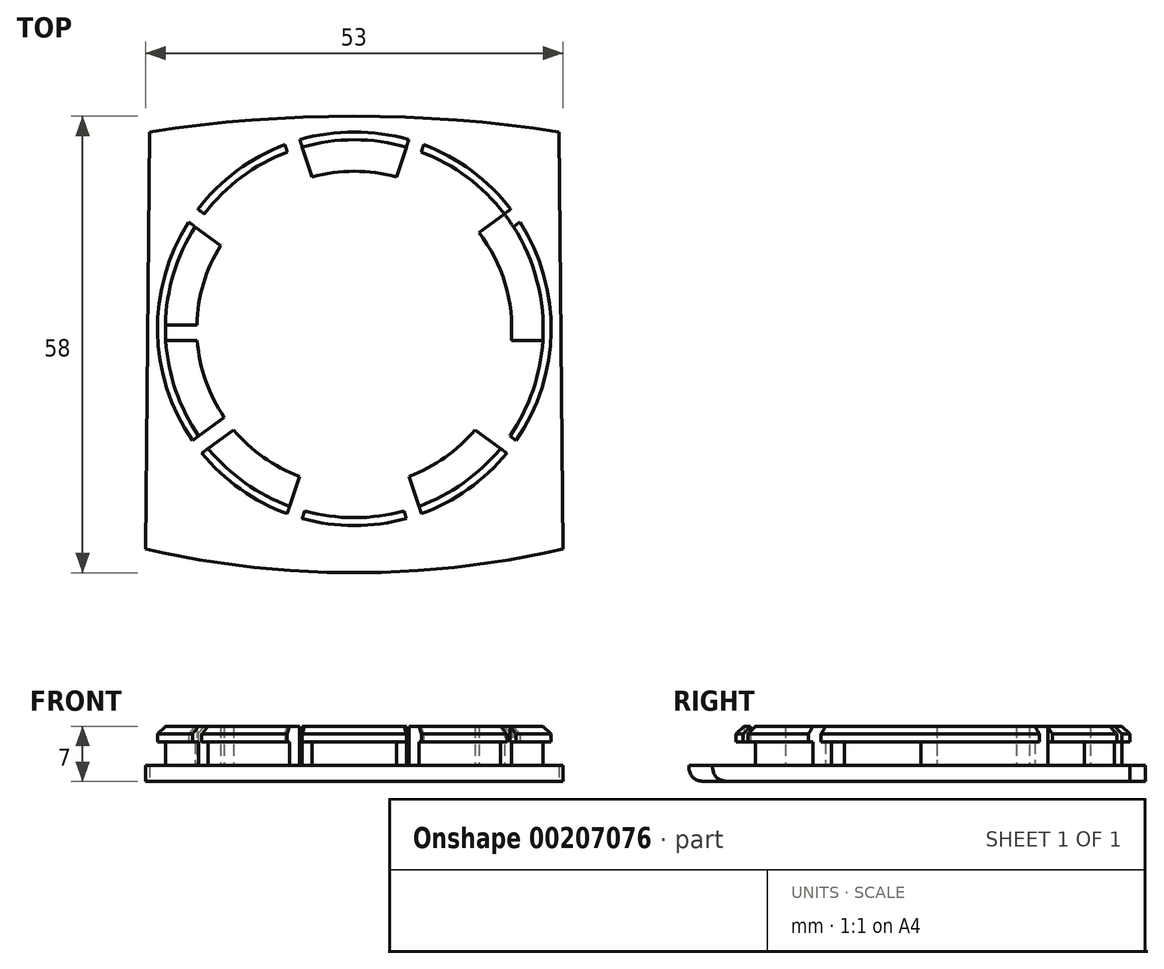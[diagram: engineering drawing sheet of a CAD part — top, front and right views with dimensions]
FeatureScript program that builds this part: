
annotation { "Feature Type Name" : "Feature", "Feature Type Description" : "" }
export const myFeature = defineFeature(function(context is Context, id is Id, definition is map)
    precondition{}
    {
        {
            var Q0;
            Q0=qCreatedBy(makeId("Top.planeOp"),FACE);
            var sketch = newSketch(context, id + "F0", { "sketchPlane" : qUnion([Q0])});
            skLineSegment(sketch, "E0", {"start": v(-26, 27.5) * mm, "end": v(-26.5, -27.5) * mm});
            skLineSegment(sketch, "E1", {"start": v(-26.5, -27.5) * mm, "end": v(26.5, -27.5) * mm, "construction": true});
            skLineSegment(sketch, "E2", {"start": v(26.5, -27.5) * mm, "end": v(26, 27.5) * mm});
            skLineSegment(sketch, "E3", {"start": v(26, 27.5) * mm, "end": v(-26, 27.5) * mm});
            skArc(sketch, "E4", {"start": v(-26.5, -27.5) * mm, "mid": v(0, -30.5) * mm, "end": v(26.5, -27.5) * mm});
            skPoint(sketch, "E5", {"position": v(0, -27.5) * mm});
            skPoint(sketch, "E6", {"position": v(0, 27.5) * mm});
            skLineSegment(sketch, "E7", {"start": v(0, 27.5) * mm, "end": v(0, -27.5) * mm, "construction": true});
            skPoint(sketch, "E8", {"position": v(-26.25, 0) * mm});
            skPoint(sketch, "E9", {"position": v(26.25, 0) * mm});
            skLineSegment(sketch, "E10", {"start": v(-26.25, 0) * mm, "end": v(26.25, 0) * mm, "construction": true});
            skPoint(sketch, "E11", {"position": v(0, 0) * mm});
            skArc(sketch, "E12", {"start": v(26.02, 25.5) * mm, "mid": v(0, 27.5) * mm, "end": v(-26.02, 25.5) * mm});
            skSolve(sketch);
        }
        {
            var Q0;
            {var subQ4=sQuery(id+"F0.wireOp",EDGE,"E4");Q0=makeQuery(id+"F0.imprint","IMPRINT",FACE,{"disambiguationData":[TD([[makeQuery(id+"F0.imprint","IMPRINT",EDGE,{"derivedFrom":subQ4}),1.0]])]});}
            extrude(context, id + "F1", {"entities" : qUnion([Q0]), "depth" : 2 * mm});
        }
        {
            var Q0;
            Q0=qCreatedBy(makeId("Top.planeOp"),FACE);
            var sketch = newSketch(context, id + "F2", { "sketchPlane" : qUnion([Q0])});
            skCircle(sketch, "E13", {"center": v(0, 0.5) * mm, "radius": 24 * mm});
            skCircle(sketch, "E14.0", {"center": v(0, 0.5) * mm, "radius": 20 * mm});
            skSolve(sketch);
        }
        {
            var Q0;
            Q0=makeQuery(id+"F2.imprint","IMPRINT",FACE,{"disambiguationData":[TD([[makeQuery(id+"F2.imprint","IMPRINT",EDGE,{"derivedFrom":sQuery(id+"F2.wireOp",EDGE,"E13")}),1.0]])]});
            extrude(context, id + "F3", {"entities" : qUnion([Q0]), "operationType" : NewBodyOperationType.ADD, "depth" : 7 * mm});
        }
        {
            var Q0;
            {var subQ0=sQuery(id+"F0.wireOp",EDGE,"E4");var subQ1=sQuery(id+"F0.wireOp",EDGE,"E3");var subQ2=sQuery(id+"F0.wireOp",EDGE,"E2");var subQ3=sQuery(id+"F0.wireOp",EDGE,"E0");Q0=makeQuery(id+"F3.boolean.opBoolean","SPLIT",FACE,{"disambiguationData":[TD([makeQuery(id+"F1.opExtrude","SWEPT_FACE",FACE,{"disambiguationData":[OSD([subQ3])]})])],"derivedFrom":makeQuery(id+"F1.opExtrude","CAP_FACE",FACE,{"disambiguationData":[OSD([subQ3,subQ2,subQ1,subQ0])],"isStart":false})});}
            cPlane(context, id + "F4", {"entities" : qUnion([Q0]), "cplaneType" : CPlaneType.OFFSET, "offset" : 3 * mm, "width" : 150 * mm, "height" : 150 * mm});
        }
        {
            var Q0;
            Q0=qCreatedBy(id+"F4.planeOp",FACE);
            var sketch = newSketch(context, id + "F5", { "sketchPlane" : qUnion([Q0])});
            skCircle(sketch, "E15.0", {"center": v(0, 0.5) * mm, "radius": 25 * mm});
            skCircle(sketch, "E16.0", {"center": v(0, 0.5) * mm, "radius": 23.82 * mm});
            skSolve(sketch);
        }
        {
            var Q0;
            Q0=makeQuery(id+"F5.imprint","IMPRINT",FACE,{"disambiguationData":[TD([[makeQuery(id+"F5.imprint","IMPRINT",EDGE,{"derivedFrom":sQuery(id+"F5.wireOp",EDGE,"E15.0")}),1.0]])]});
            extrude(context, id + "F6", {"entities" : qUnion([Q0]), "operationType" : NewBodyOperationType.ADD, "depth" : 2 * mm});
        }
        {
            var Q0;
            Q0=makeQuery(id+"F6.opExtrude","CAP_EDGE",EDGE,{"disambiguationData":[OSD([sQuery(id+"F5.wireOp",EDGE,"E15.0")])],"isStart":false});
            chamfer(context, id + "F7", {"entities" : qUnion([Q0]), "width" : 1 * mm, "tangentPropagation" : true});
        }
        {
            var Q0;
            {var subQ0=sQuery(id+"F0.wireOp",EDGE,"E4");var subQ1=sQuery(id+"F0.wireOp",EDGE,"E3");var subQ2=sQuery(id+"F0.wireOp",EDGE,"E2");var subQ3=sQuery(id+"F0.wireOp",EDGE,"E0");Q0=makeQuery(id+"F3.boolean.opBoolean","SPLIT",FACE,{"disambiguationData":[TD([makeQuery(id+"F1.opExtrude","SWEPT_FACE",FACE,{"disambiguationData":[OSD([subQ3])]})])],"derivedFrom":makeQuery(id+"F1.opExtrude","CAP_FACE",FACE,{"disambiguationData":[OSD([subQ3,subQ2,subQ1,subQ0])],"isStart":false})});}
            var sketch = newSketch(context, id + "F8", { "sketchPlane" : qUnion([Q0])});
            skLineSegment(sketch, "E17.bottom", {"start": v(26, 1) * mm, "end": v(-26, 1) * mm});
            skLineSegment(sketch, "E17.top", {"start": v(26, -1) * mm, "end": v(-26, -1) * mm});
            skLineSegment(sketch, "E17.left", {"start": v(26, 1) * mm, "end": v(26, -1) * mm});
            skLineSegment(sketch, "E17.right", {"start": v(-26, 1) * mm, "end": v(-26, -1) * mm});
            skPoint(sketch, "E17.middle", {"position": v(0, 0) * mm});
            skLineSegment(sketch, "E18.1.0", {"start": v(21.62, -14.47) * mm, "end": v(-20.45, 16.1) * mm});
            skLineSegment(sketch, "E18.1.1", {"start": v(20.45, -16.1) * mm, "end": v(-21.62, 14.47) * mm});
            skLineSegment(sketch, "E18.1.2", {"start": v(-20.45, 16.1) * mm, "end": v(-21.62, 14.47) * mm});
            skLineSegment(sketch, "E18.1.3", {"start": v(21.62, -14.47) * mm, "end": v(20.45, -16.1) * mm});
            skLineSegment(sketch, "E18.2.0", {"start": v(8.99, -24.42) * mm, "end": v(-7.08, 25.04) * mm});
            skLineSegment(sketch, "E18.2.1", {"start": v(7.08, -25.04) * mm, "end": v(-8.99, 24.42) * mm});
            skLineSegment(sketch, "E18.2.2", {"start": v(-7.08, 25.04) * mm, "end": v(-8.99, 24.42) * mm});
            skLineSegment(sketch, "E18.2.3", {"start": v(8.99, -24.42) * mm, "end": v(7.08, -25.04) * mm});
            skLineSegment(sketch, "E18.3.0", {"start": v(-7.08, -25.04) * mm, "end": v(8.99, 24.42) * mm});
            skLineSegment(sketch, "E18.3.1", {"start": v(-8.99, -24.42) * mm, "end": v(7.08, 25.04) * mm});
            skLineSegment(sketch, "E18.3.2", {"start": v(8.99, 24.42) * mm, "end": v(7.08, 25.04) * mm});
            skLineSegment(sketch, "E18.3.3", {"start": v(-7.08, -25.04) * mm, "end": v(-8.99, -24.42) * mm});
            skLineSegment(sketch, "E18.4.0", {"start": v(-20.45, -16.1) * mm, "end": v(21.62, 14.47) * mm});
            skLineSegment(sketch, "E18.4.1", {"start": v(-21.62, -14.47) * mm, "end": v(20.45, 16.1) * mm});
            skLineSegment(sketch, "E18.4.2", {"start": v(21.62, 14.47) * mm, "end": v(20.45, 16.1) * mm});
            skLineSegment(sketch, "E18.4.3", {"start": v(-20.45, -16.1) * mm, "end": v(-21.62, -14.47) * mm});
            skLineSegment(sketch, "E18.5.0", {"start": v(-26, -1) * mm, "end": v(26, -1) * mm});
            skLineSegment(sketch, "E18.5.1", {"start": v(-26, 1) * mm, "end": v(26, 1) * mm});
            skLineSegment(sketch, "E18.5.2", {"start": v(26, -1) * mm, "end": v(26, 1) * mm});
            skLineSegment(sketch, "E18.5.3", {"start": v(-26, -1) * mm, "end": v(-26, 1) * mm});
            skLineSegment(sketch, "E18.anchor1", {"start": v(0, 0) * mm, "end": v(-26, -1) * mm, "construction": true});
            skLineSegment(sketch, "E18.anchor2", {"start": v(0, 0) * mm, "end": v(26, 1) * mm, "construction": true});
            skSolve(sketch);
        }
        {
            var Q0;
            {var subQ0=sQuery(id+"F8.wireOp",EDGE,"E18.2.1");var subQ1=sQuery(id+"F8.wireOp",EDGE,"E18.1.0");var subQ2=makeQuery(id+"F8.imprint","INTERSECT",VERTEX,{"derivedFrom":[subQ1,subQ0]});Q0=makeQuery(id+"F8.imprint","IMPRINT",FACE,{"disambiguationData":[TD([[makeQuery(id+"F8.imprint","IMPRINT",EDGE,{"disambiguationData":[TD([[subQ2,1.0]])],"derivedFrom":subQ0}),1.0]])]});}
            var Q1;
            {var subQ1=sQuery(id+"F8.wireOp",EDGE,"E18.2.0");var subQ5=sQuery(id+"F8.wireOp",EDGE,"E18.4.1");var subQ9=makeQuery(id+"F8.imprint","INTERSECT",VERTEX,{"derivedFrom":[subQ1,subQ5]});Q1=makeQuery(id+"F8.imprint","IMPRINT",FACE,{"disambiguationData":[TD([[makeQuery(id+"F8.imprint","IMPRINT",EDGE,{"disambiguationData":[TD([[subQ9,-1.0]])],"derivedFrom":subQ1}),-1.0]])]});}
            var Q2;
            {var subQ1=sQuery(id+"F8.wireOp",EDGE,"E18.1.0");var subQ5=sQuery(id+"F8.wireOp",EDGE,"E18.3.1");var subQ9=makeQuery(id+"F8.imprint","INTERSECT",VERTEX,{"derivedFrom":[subQ1,subQ5]});Q2=makeQuery(id+"F8.imprint","IMPRINT",FACE,{"disambiguationData":[TD([[makeQuery(id+"F8.imprint","IMPRINT",EDGE,{"disambiguationData":[TD([[subQ9,-1.0]])],"derivedFrom":subQ1}),-1.0]])]});}
            var Q3;
            {var subQ0=sQuery(id+"F8.wireOp",EDGE,"E18.5.1");var subQ1=sQuery(id+"F8.wireOp",EDGE,"E18.3.0");var subQ2=makeQuery(id+"F8.imprint","INTERSECT",VERTEX,{"derivedFrom":[subQ1,subQ0]});Q3=makeQuery(id+"F8.imprint","IMPRINT",FACE,{"disambiguationData":[TD([[makeQuery(id+"F8.imprint","IMPRINT",EDGE,{"disambiguationData":[TD([[subQ2,-1.0]])],"derivedFrom":subQ1}),-1.0]])]});}
            var Q4;
            {var subQ0=sQuery(id+"F8.wireOp",EDGE,"E18.5.0");var subQ1=sQuery(id+"F8.wireOp",EDGE,"E18.1.0");var subQ2=makeQuery(id+"F8.imprint","INTERSECT",VERTEX,{"derivedFrom":[subQ1,subQ0]});Q4=makeQuery(id+"F8.imprint","IMPRINT",FACE,{"disambiguationData":[TD([[makeQuery(id+"F8.imprint","IMPRINT",EDGE,{"disambiguationData":[TD([[subQ2,-1.0]])],"derivedFrom":subQ1}),-1.0]])]});}
            var Q5;
            {var subQ3=sQuery(id+"F8.wireOp",EDGE,"E18.2.0");var subQ5=sQuery(id+"F8.wireOp",EDGE,"E18.1.1");var subQ6=makeQuery(id+"F8.imprint","INTERSECT",VERTEX,{"derivedFrom":[subQ5,subQ3]});Q5=makeQuery(id+"F8.imprint","IMPRINT",FACE,{"disambiguationData":[TD([[makeQuery(id+"F8.imprint","IMPRINT",EDGE,{"disambiguationData":[TD([[subQ6,-1.0]])],"derivedFrom":subQ3}),-1.0]])]});}
            var Q6;
            {var subQ1=sQuery(id+"F8.wireOp",EDGE,"E18.2.1");var subQ5=sQuery(id+"F8.wireOp",EDGE,"E18.3.0");var subQ9=makeQuery(id+"F8.imprint","INTERSECT",VERTEX,{"derivedFrom":[subQ1,subQ5]});Q6=makeQuery(id+"F8.imprint","IMPRINT",FACE,{"disambiguationData":[TD([[makeQuery(id+"F8.imprint","IMPRINT",EDGE,{"disambiguationData":[TD([[subQ9,-1.0]])],"derivedFrom":subQ1}),1.0]])]});}
            var Q7;
            {var subQ1=sQuery(id+"F8.wireOp",EDGE,"E18.1.1");var subQ7=sQuery(id+"F8.wireOp",EDGE,"E18.2.0");var subQ8=makeQuery(id+"F8.imprint","INTERSECT",VERTEX,{"derivedFrom":[subQ1,subQ7]});Q7=makeQuery(id+"F8.imprint","IMPRINT",FACE,{"disambiguationData":[TD([[makeQuery(id+"F8.imprint","IMPRINT",EDGE,{"disambiguationData":[TD([[subQ8,-1.0]])],"derivedFrom":subQ1}),1.0]])]});}
            var Q8;
            {var subQ1=sQuery(id+"F8.wireOp",EDGE,"E18.3.1");var subQ7=sQuery(id+"F8.wireOp",EDGE,"E18.4.0");var subQ8=makeQuery(id+"F8.imprint","INTERSECT",VERTEX,{"derivedFrom":[subQ1,subQ7]});Q8=makeQuery(id+"F8.imprint","IMPRINT",FACE,{"disambiguationData":[TD([[makeQuery(id+"F8.imprint","IMPRINT",EDGE,{"disambiguationData":[TD([[subQ8,-1.0]])],"derivedFrom":subQ1}),1.0]])]});}
            var Q9;
            {var subQ1=sQuery(id+"F8.wireOp",EDGE,"E18.4.1");var subQ6=sQuery(id+"F8.wireOp",EDGE,"E18.1.1");var subQ9=makeQuery(id+"F8.imprint","INTERSECT",VERTEX,{"derivedFrom":[subQ6,subQ1]});Q9=makeQuery(id+"F8.imprint","IMPRINT",FACE,{"disambiguationData":[TD([[makeQuery(id+"F8.imprint","IMPRINT",EDGE,{"disambiguationData":[TD([[subQ9,-1.0]])],"derivedFrom":subQ6}),1.0]])]});}
            var Q10;
            {var subQ0=sQuery(id+"F8.wireOp",EDGE,"E18.4.3");Q10=makeQuery(id+"F8.imprint","IMPRINT",FACE,{"disambiguationData":[TD([[makeQuery(id+"F8.imprint","IMPRINT",EDGE,{"derivedFrom":subQ0}),-1.0]])]});}
            var Q11;
            {var subQ0=sQuery(id+"F8.wireOp",EDGE,"E18.3.3");Q11=makeQuery(id+"F8.imprint","IMPRINT",FACE,{"disambiguationData":[TD([[makeQuery(id+"F8.imprint","IMPRINT",EDGE,{"derivedFrom":subQ0}),-1.0]])]});}
            var Q12;
            {var subQ0=sQuery(id+"F8.wireOp",EDGE,"E18.2.3");Q12=makeQuery(id+"F8.imprint","IMPRINT",FACE,{"disambiguationData":[TD([[makeQuery(id+"F8.imprint","IMPRINT",EDGE,{"derivedFrom":subQ0}),-1.0]])]});}
            var Q13;
            {var subQ0=sQuery(id+"F8.wireOp",EDGE,"E18.1.3");Q13=makeQuery(id+"F8.imprint","IMPRINT",FACE,{"disambiguationData":[TD([[makeQuery(id+"F8.imprint","IMPRINT",EDGE,{"derivedFrom":subQ0}),-1.0]])]});}
            var Q14;
            {var subQ0=sQuery(id+"F8.wireOp",EDGE,"E18.5.2");Q14=makeQuery(id+"F8.imprint","IMPRINT",FACE,{"disambiguationData":[TD([[makeQuery(id+"F8.imprint","IMPRINT",EDGE,{"derivedFrom":subQ0}),1.0]])]});}
            var Q15;
            {var subQ0=sQuery(id+"F8.wireOp",EDGE,"E18.4.2");Q15=makeQuery(id+"F8.imprint","IMPRINT",FACE,{"disambiguationData":[TD([[makeQuery(id+"F8.imprint","IMPRINT",EDGE,{"derivedFrom":subQ0}),1.0]])]});}
            var Q16;
            {var subQ0=sQuery(id+"F8.wireOp",EDGE,"E18.3.2");Q16=makeQuery(id+"F8.imprint","IMPRINT",FACE,{"disambiguationData":[TD([[makeQuery(id+"F8.imprint","IMPRINT",EDGE,{"derivedFrom":subQ0}),1.0]])]});}
            var Q17;
            {var subQ0=sQuery(id+"F8.wireOp",EDGE,"E18.2.2");Q17=makeQuery(id+"F8.imprint","IMPRINT",FACE,{"disambiguationData":[TD([[makeQuery(id+"F8.imprint","IMPRINT",EDGE,{"derivedFrom":subQ0}),1.0]])]});}
            var Q18;
            {var subQ0=sQuery(id+"F8.wireOp",EDGE,"E18.1.2");Q18=makeQuery(id+"F8.imprint","IMPRINT",FACE,{"disambiguationData":[TD([[makeQuery(id+"F8.imprint","IMPRINT",EDGE,{"derivedFrom":subQ0}),1.0]])]});}
            var Q19;
            {var subQ0=sQuery(id+"F8.wireOp",EDGE,"E18.5.3");Q19=makeQuery(id+"F8.imprint","IMPRINT",FACE,{"disambiguationData":[TD([[makeQuery(id+"F8.imprint","IMPRINT",EDGE,{"derivedFrom":subQ0}),-1.0]])]});}
            extrude(context, id + "F9", {"entities" : qUnion([Q0, Q1, Q2, Q3, Q4, Q5, Q6, Q7, Q8, Q9, Q10, Q11, Q12, Q13, Q14, Q15, Q16, Q17, Q18, Q19]), "operationType" : NewBodyOperationType.REMOVE, "depth" : 5 * mm});
        }
        {
            var Q0;
            Q0=makeQuery(id+"F1.opExtrude","CAP_EDGE",EDGE,{"disambiguationData":[OSD([sQuery(id+"F0.wireOp",EDGE,"E4")])],"isStart":true});
            fillet(context, id + "F10", {"entities" : qUnion([Q0]), "radius" : 2 * mm, "tangentPropagation" : true, "rho" : .5, "crossSection" : FilletCrossSection.CONIC, "allowEdgeOverflow" : false});
        }
    });
